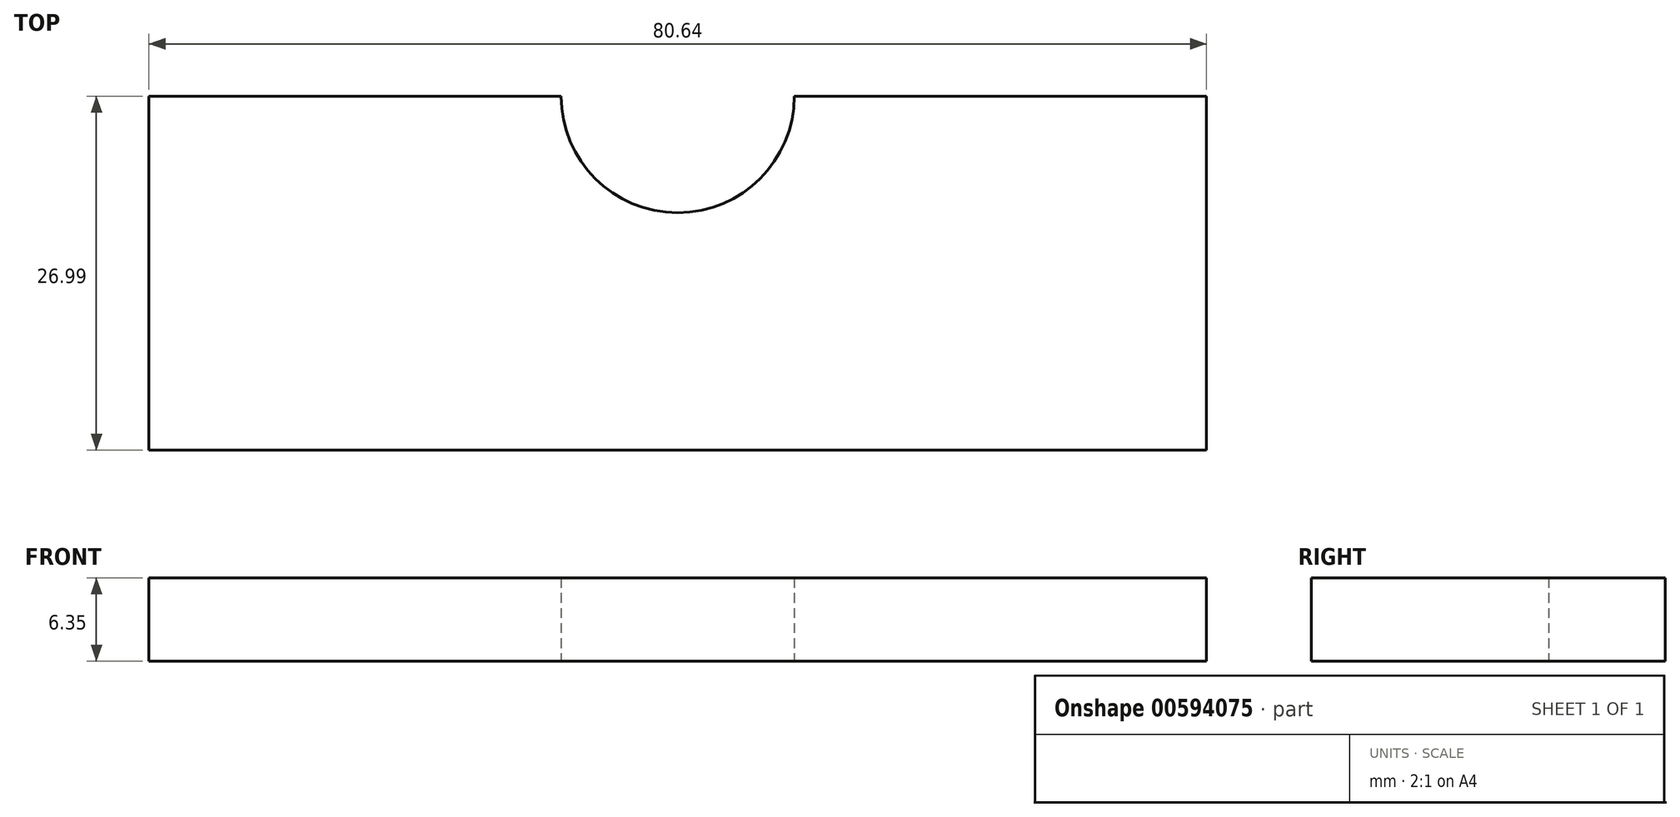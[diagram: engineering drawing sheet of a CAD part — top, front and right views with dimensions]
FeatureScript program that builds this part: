
annotation { "Feature Type Name" : "Feature", "Feature Type Description" : "" }
export const myFeature = defineFeature(function(context is Context, id is Id, definition is map)
    precondition{}
    {
        {
            var Q0;
            Q0=qCreatedBy(makeId("Top.planeOp"),FACE);
            var sketch = newSketch(context, id + "F0", { "sketchPlane" : qUnion([Q0])});
            skLineSegment(sketch, "E0.bottom", {"start": v(0, 0) * mm, "end": v(31.43, 0) * mm});
            skLineSegment(sketch, "E0.top", {"start": v(0, -26.99) * mm, "end": v(80.65, -26.99) * mm});
            skLineSegment(sketch, "E0.left", {"start": v(0, 0) * mm, "end": v(0, -26.99) * mm});
            skLineSegment(sketch, "E0.right", {"start": v(80.65, 0) * mm, "end": v(80.65, -26.99) * mm});
            skArc(sketch, "E1", {"start": v(31.43, 0) * mm, "mid": v(40.32, -8.9) * mm, "end": v(49.21, 0) * mm});
            skLineSegment(sketch, "E2.trimOffspring", {"start": v(49.21, 0) * mm, "end": v(80.65, 0) * mm});
            skSolve(sketch);
        }
        {
            var Q0;
            Q0=makeQuery(id+"F0.imprint","IMPRINT",FACE,{"disambiguationData":[TD([[makeQuery(id+"F0.imprint","IMPRINT",EDGE,{"derivedFrom":sQuery(id+"F0.wireOp",EDGE,"E0.bottom")}),-1.0]])]});
            extrude(context, id + "F1", {"entities" : qUnion([Q0]), "depth" : 6.35 * mm, "offsetDistance" : 25.4 * mm});
        }
    });
